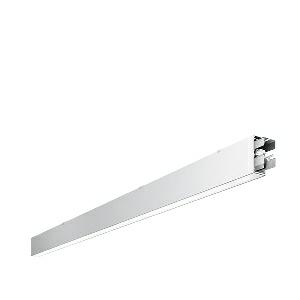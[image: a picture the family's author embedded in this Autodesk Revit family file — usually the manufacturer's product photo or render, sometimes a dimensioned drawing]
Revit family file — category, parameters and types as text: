
# Revit family: dotoo_line_-_dla_3000_830_d_mid_00807947_02ea
name_source: partatom
category: Lighting Fixtures
units: mm (PartAtom-declared; Revit-internal decimal feet)

## family parameters
Cut with Voids When Loaded = No
Host = Face
Light Source = No
Part Type = Normal
Room Calculation Point = No
Round Connector Dimension = Use Diameter
Shared = No

## types (1)
- DOTOO.line - DLA 3000/830/D MID (1 x LED, 2650 lm, 3000K)
    Apparent Load = 26 VA
    Approval mark = CE
    CIE Flux Codes = 67 91 98 100 100
    Color Rendering = 80-89
    Color Temperature = 3000K
    Control Gear = Electronic ballast
    Default Elevation = 1800 mm
    Description = DLA 3000/830/D|Surface-mounted luminaire.|light source: LED|work equipment: Adjustable electronic ballast, digital DALI|connected load: 220-240 V, 50/60 Hz|Power consumption: approx. 26 W|luminous flux: 2650 lm|luminous efficacy: 101 lm/W|light distribution: Direct|colour temperature: Warm white, ca. 3000 K|class of protection: I|technology: Continuously dimmable|mains lead: Connector|glare control: Prism aperture|special features: DALI Load 1x, TouchDIM - dimming via standard switch, Through-wired, up to 18 m on one mains connection, Flicker-free, Suitable as emergency lighting, Mechanical and electrical connection of the individual modules without tools|
    Frequency = 50 Hz
    Height = 110 mm
    Lamp = 1 x LED
    Lamp Light Flux = 2650 lm
    Lamp count = 1
    Length = 2244 mm
    Luminous efficacy = 102 lm/W
    Manufacturer = Waldmann
    ModVariant = No
    Model = 00807947
    Mounting Place = Ceiling
    Mounting Type = Surface mounted
    Number of Poles = 1
    OnlyDefault = Yes
    Power Factor = 1
    Product Name = DOTOO.line - DLA 3000/830/D MID
    Product group = Ceiling mounted luminaire
    ProductGroupID = 3
    Protection Class = Protection class I
    Protection Degree = IP 40
    RLX_Detail_Level = 1
    RLX_Emergency_Light_Flux = 0 lm
    RLX_Emergency_Type = 0
    RLX_Emergency_Type_DB = No
    RlxData = <blob elided: 20429 chars, md5=a254a4c4>
    Socket = socket
    Standby Power = 0 W
    System Light Flux = 2650 lm
    System Power = 26 W
    Type Comments = Product without accessories
    Type Image = 114358000-00807935.jpg
    URL = http://relux.com
    VarID = ---
    Voltage = 230 V
    Voltage Range = 220-240 V
    Weight = 0.00 kg
    Width = 60 mm  [stored 0.19685 ft]

note: [stored X ft] marks values corroborated as IEEE doubles in the binary element streams (Revit-internal decimal feet)

## geometry (parser evidence)
native form markers: Blend x4, Sweep x12
no freeform markers — native parametric forms only
